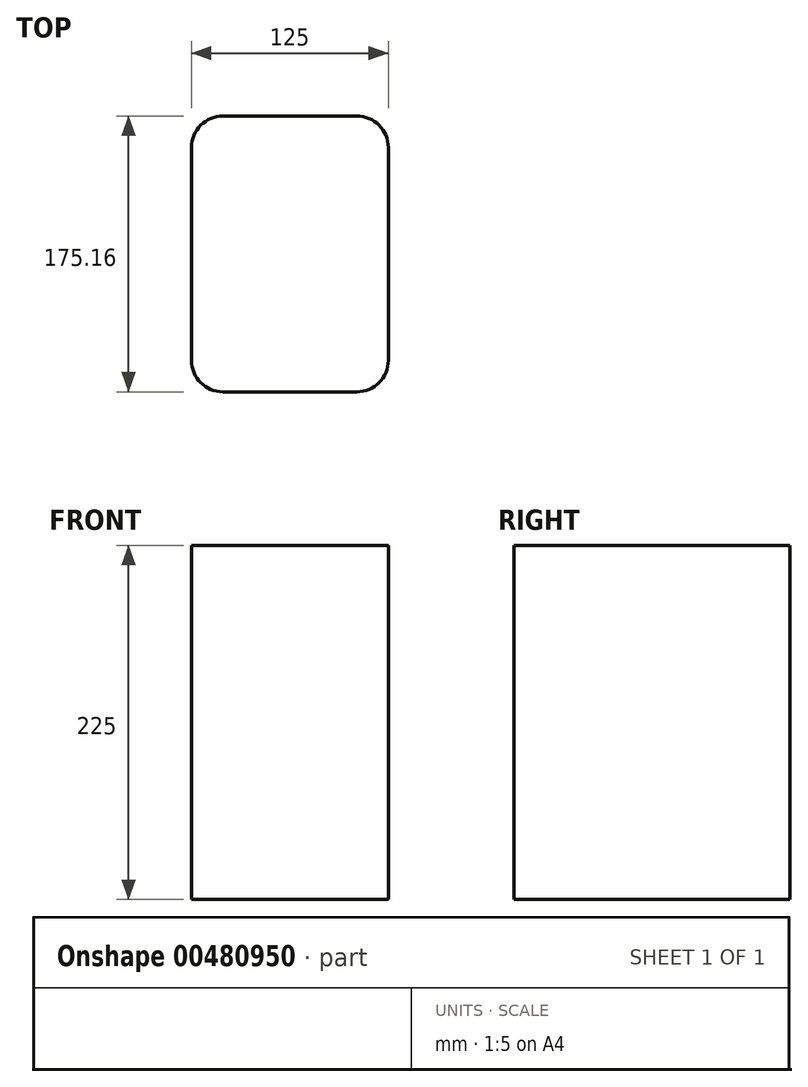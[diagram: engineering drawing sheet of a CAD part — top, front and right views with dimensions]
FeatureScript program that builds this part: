
annotation { "Feature Type Name" : "Feature", "Feature Type Description" : "" }
export const myFeature = defineFeature(function(context is Context, id is Id, definition is map)
    precondition{}
    {
        {
            var Q0;
            Q0=qCreatedBy(makeId("Top.planeOp"),FACE);
            var sketch = newSketch(context, id + "F0", { "sketchPlane" : qUnion([Q0])});
            skLineSegment(sketch, "E0", {"start": v(-116, 95.54) * mm, "end": v(-31, 95.54) * mm});
            skLineSegment(sketch, "E1", {"start": v(-11, 75.54) * mm, "end": v(-11, -59.62) * mm});
            skLineSegment(sketch, "E2", {"start": v(-31, -79.62) * mm, "end": v(-116, -79.62) * mm});
            skPoint(sketch, "E3.visualSharp", {"position": v(-11, 95.54) * mm});
            skArc(sketch, "E3.filletArc", {"start": v(-11, 75.54) * mm, "mid": v(-16.86, 89.69) * mm, "end": v(-31, 95.54) * mm});
            skPoint(sketch, "E4.visualSharp", {"position": v(-11, -79.62) * mm});
            skArc(sketch, "E4.filletArc", {"start": v(-31, -79.62) * mm, "mid": v(-16.86, -73.76) * mm, "end": v(-11, -59.62) * mm});
            skLineSegment(sketch, "E5", {"start": v(-136, -59.62) * mm, "end": v(-136, 75.54) * mm});
            skArc(sketch, "E6.filletArc", {"start": v(-116, 95.54) * mm, "mid": v(-130.14, 89.69) * mm, "end": v(-136, 75.54) * mm});
            skPoint(sketch, "E7.visualSharp", {"position": v(-136, -79.62) * mm});
            skArc(sketch, "E7.filletArc", {"start": v(-136, -59.62) * mm, "mid": v(-130.14, -73.76) * mm, "end": v(-116, -79.62) * mm});
            skSolve(sketch);
        }
        {
            var Q0;
            Q0=qSketchRegion(id+"F0",true);
            extrude(context, id + "F1", {"entities" : qUnion([Q0]), "depth" : 225 * mm});
        }
    });
